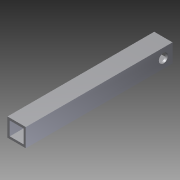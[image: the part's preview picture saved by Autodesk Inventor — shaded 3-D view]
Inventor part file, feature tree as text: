
AUTODESK INVENTOR PART (.ipt)
format: ipt  version: 2012 (Build 160160000, 160)  size: 87,552 bytes
history: native  units: in
note: dims shown in document units (in); Inventor stores cm internally (conversion verified against a paired STEP export)
features: extrude x2, sketch x2
ambient origin geometry x8: Origin, YZ Plane, XZ Plane, XY Plane, X Axis, Y Axis, Z Axis, Center Point
bodies: Solid1 (feature_tree)
feature tree (4):
  extrude  "Extrusion1"  Depth=0.125in
  extrude  "Extrusion2"  Depth=0.125in
  sketch  "Sketch1"  dims[d0=0.125in d1=0.125in]
  sketch  "Sketch2"  dims[d2=0.125in d3=0.125in d4=1.0in d5=1.0in d6=8.0in d7=0.0in d8=0.5in d9=0.5in d10=0.5in d11=8.0in d12=0.0in]
